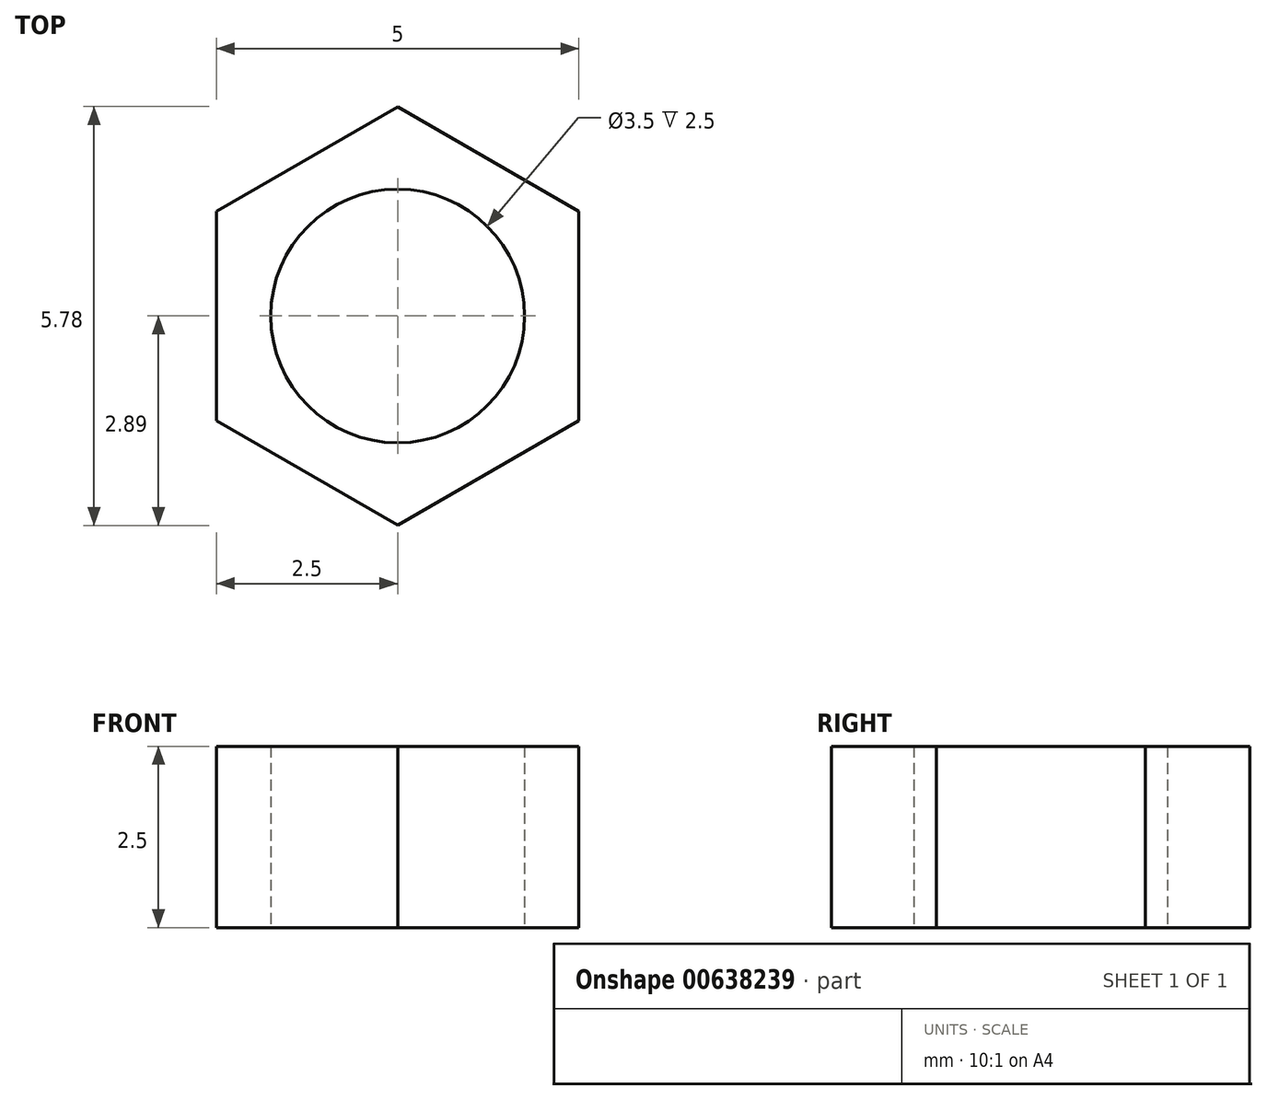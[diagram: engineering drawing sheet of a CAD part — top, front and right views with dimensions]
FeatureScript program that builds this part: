
annotation { "Feature Type Name" : "Feature", "Feature Type Description" : "" }
export const myFeature = defineFeature(function(context is Context, id is Id, definition is map)
    precondition{}
    {
        {
            var Q0;
            Q0=qCreatedBy(makeId("Top.planeOp"),FACE);
            var sketch = newSketch(context, id + "F0", { "sketchPlane" : qUnion([Q0])});
            skCircle(sketch, "E0", {"center": v(0, 0) * mm, "radius": 1.75 * mm});
            skCircle(sketch, "E1.cCircle", {"center": v(0, 0) * mm, "radius": 2.5 * mm, "construction": true});
            skLineSegment(sketch, "E1.0", {"start": v(-2.5, -1.44) * mm, "end": v(-2.5, 1.44) * mm});
            skLineSegment(sketch, "E1.1", {"start": v(-2.5, 1.44) * mm, "end": v(0, 2.89) * mm});
            skLineSegment(sketch, "E1.2", {"start": v(0, 2.89) * mm, "end": v(2.5, 1.44) * mm});
            skLineSegment(sketch, "E1.3", {"start": v(2.5, 1.44) * mm, "end": v(2.5, -1.44) * mm});
            skLineSegment(sketch, "E1.4", {"start": v(2.5, -1.44) * mm, "end": v(0, -2.89) * mm});
            skLineSegment(sketch, "E1.5", {"start": v(0, -2.89) * mm, "end": v(-2.5, -1.44) * mm});
            skPoint(sketch, "E1.0.midPoint", {"position": v(-2.5, 0) * mm});
            skSolve(sketch);
        }
        {
            var Q0;
            Q0=makeQuery(id+"F0.imprint","IMPRINT",FACE,{"disambiguationData":[TD([[makeQuery(id+"F0.imprint","IMPRINT",EDGE,{"derivedFrom":sQuery(id+"F0.wireOp",EDGE,"E0")}),-1.0]])]});
            extrude(context, id + "F1", {"entities" : qUnion([Q0]), "depth" : 2.5 * mm, "offsetDistance" : 25 * mm});
        }
    });
